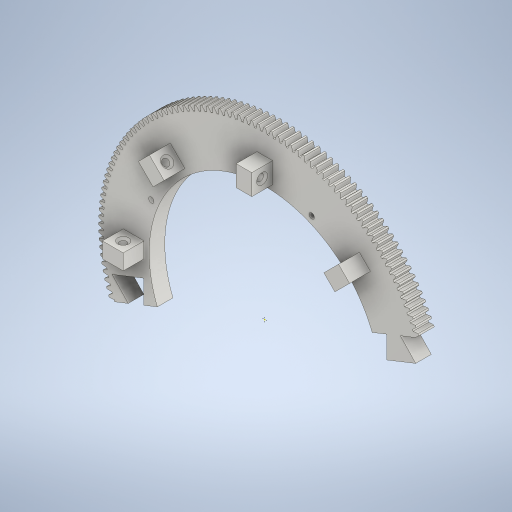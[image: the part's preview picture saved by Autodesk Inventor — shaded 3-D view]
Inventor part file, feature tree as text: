
AUTODESK INVENTOR PART (.ipt)
format: ipt  version: 2023 (Build 270158000, 158)  size: 2,501,120 bytes
history: native  units: mm (DEFAULTED — no unit token found)
features: sketch x7, extrude x5, plane x3, other x3, pattern_circular x2, chamfer x1, hole x1, projected_geometry x1
ambient origin geometry x8: Origin, YZ Plane, XZ Plane, XY Plane, X Axis, Y Axis, Z Axis, Center Point
bodies: Solid1 (feature_tree)
feature tree (23):
  extrude  "Extrusion1"  Depth=15.0mm TaperAngle=0.0deg
  plane  "Work Plane2"
  plane  "Work Plane8"
  plane  "Work Plane9"
  other  "Spur Gear"
  extrude  "Extrusion2"  Depth=10.0mm TaperAngle=0.0deg
  extrude  "Extrusion4"  Depth=0.19635mm TaperAngle=0.0deg
  extrude  "Extrusion5"  TaperAngle=0.0deg  [1 undecoded]
  chamfer  "Chamfer1"  [1 undecoded]
  pattern_circular  "Circular Pattern3"  Count=25  [1 undecoded]
  hole  "Hole2"  [1 undecoded]
  pattern_circular  "Circular Pattern4"  [2 undecoded]
  extrude  "Extrusion7"  Depth=20.0mm
  sketch  "Sketch12"  dims[d50=222.5mm d51=15.0mm d52=0.0mm d75=7.5mm d76=20.0mm d77=15.0mm d78=20.0mm d79=20.0mm d80=0.0mm d81=6.5mm d82=20.0mm d83=0.0mm d87=2.0mm d88=2.0mm d89=45.0deg d90=80.0mm d91=360.0deg d110=5.0mm d111=67.5deg d112=5.0mm d113=6.0mm d114=4.0mm d115=2.0mm d116=90.0deg d117=8.0mm d118=20.594885mm d119=40.0mm d120=360.0deg d123=22.125mm d124=20.0mm d125=15.0mm d126=1.0mm d127=1.0mm d128=4.0mm d129=50.0mm d130=0.0mm d106=0.5mm d107=0.872665mm d108=0.5mm d109=0.872665mm]
  sketch  "Sketch1"  dims[d0=320.0mm d1=15.0mm d2=0.0mm]
  sketch  "Sketch2"  dims[d3=320.0mm d4=10.0mm d5=0.0mm]
  other  "Srf1"
  sketch  "Sketch3"  dims[d16=200.0mm d17=0.0mm d34=0.19635mm]
  sketch  "Sketch7"  dims[d39=0.0mm d41=0.0mm]
  sketch  "Sketch8"  dims[d43=200.0mm]
  sketch  "Sketch11"  dims[d46=200.0mm d47=0.0mm d48=0.0mm d49=250.0mm]
  projected_geometry  "Projected Loop3"
  other  "Pitch Diameter"
note: 6 required parameter values undecoded (feature->parameter linkage not recoverable at this tier; creation-order binding heuristic only, values carry confidence <= 0.55)
